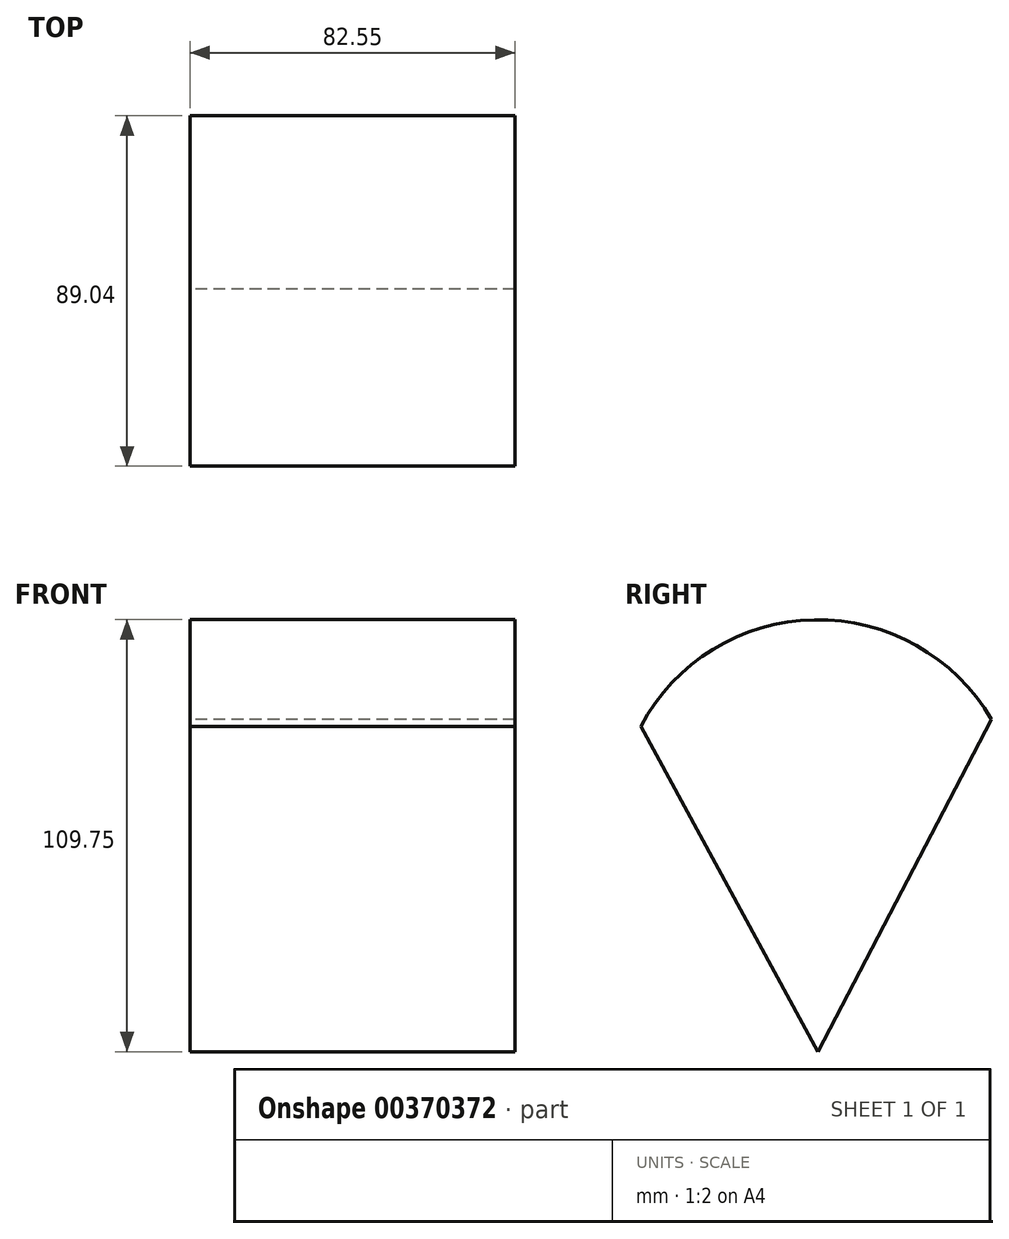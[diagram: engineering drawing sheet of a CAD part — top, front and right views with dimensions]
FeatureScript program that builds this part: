
annotation { "Feature Type Name" : "Feature", "Feature Type Description" : "" }
export const myFeature = defineFeature(function(context is Context, id is Id, definition is map)
    precondition{}
    {
        {
            var Q0;
            Q0=qCreatedBy(makeId("Right.planeOp"),FACE);
            var sketch = newSketch(context, id + "F0", { "sketchPlane" : qUnion([Q0])});
            skArc(sketch, "E0", {"start": v(44.05, 38.85) * mm, "mid": v(-0.97, 64.2) * mm, "end": v(-45, 37.15) * mm});
            skLineSegment(sketch, "E1", {"start": v(-45, 37.15) * mm, "end": v(0, -45.54) * mm});
            skLineSegment(sketch, "E2", {"start": v(0, -45.54) * mm, "end": v(44.05, 38.85) * mm});
            skSolve(sketch);
        }
        {
            var Q0;
            Q0 = qSketchRegion(id + "F0", true);
            extrude(context, id + "F1", {"entities" : qUnion([Q0]), "depth" : 82.55 * mm});
        }
    });
